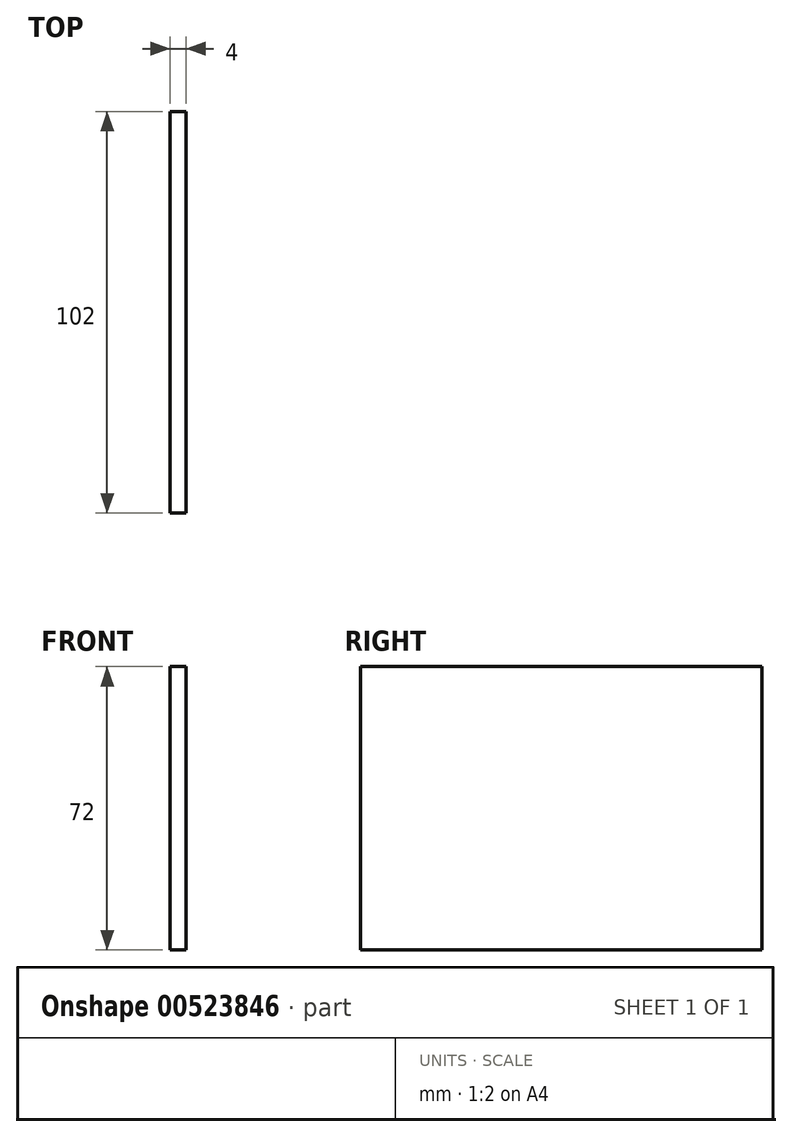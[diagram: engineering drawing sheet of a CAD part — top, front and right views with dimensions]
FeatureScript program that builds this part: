
annotation { "Feature Type Name" : "Feature", "Feature Type Description" : "" }
export const myFeature = defineFeature(function(context is Context, id is Id, definition is map)
    precondition{}
    {
        {
            var Q0;
            Q0=qCreatedBy(makeId("Right.planeOp"),FACE);
            var sketch = newSketch(context, id + "F0", { "sketchPlane" : qUnion([Q0])});
            skLineSegment(sketch, "E0.bottom", {"start": v(-51, 36) * mm, "end": v(51, 36) * mm});
            skLineSegment(sketch, "E0.top", {"start": v(-51, -36) * mm, "end": v(51, -36) * mm});
            skLineSegment(sketch, "E0.left", {"start": v(-51, 36) * mm, "end": v(-51, -36) * mm});
            skLineSegment(sketch, "E0.right", {"start": v(51, 36) * mm, "end": v(51, -36) * mm});
            skPoint(sketch, "E0.middle", {"position": v(0, 0) * mm});
            skSolve(sketch);
        }
        {
            var Q0;
            Q0=makeQuery(id+"F0.imprint","IMPRINT",FACE,{"disambiguationData":[TD([[makeQuery(id+"F0.imprint","IMPRINT",EDGE,{"derivedFrom":sQuery(id+"F0.wireOp",EDGE,"E0.bottom")}),-1.0]])]});
            extrude(context, id + "F1", {"entities" : qUnion([Q0]), "endBound" : BoundingType.SYMMETRIC, "depth" : 4 * mm, "offsetDistance" : 25 * mm});
        }
    });
